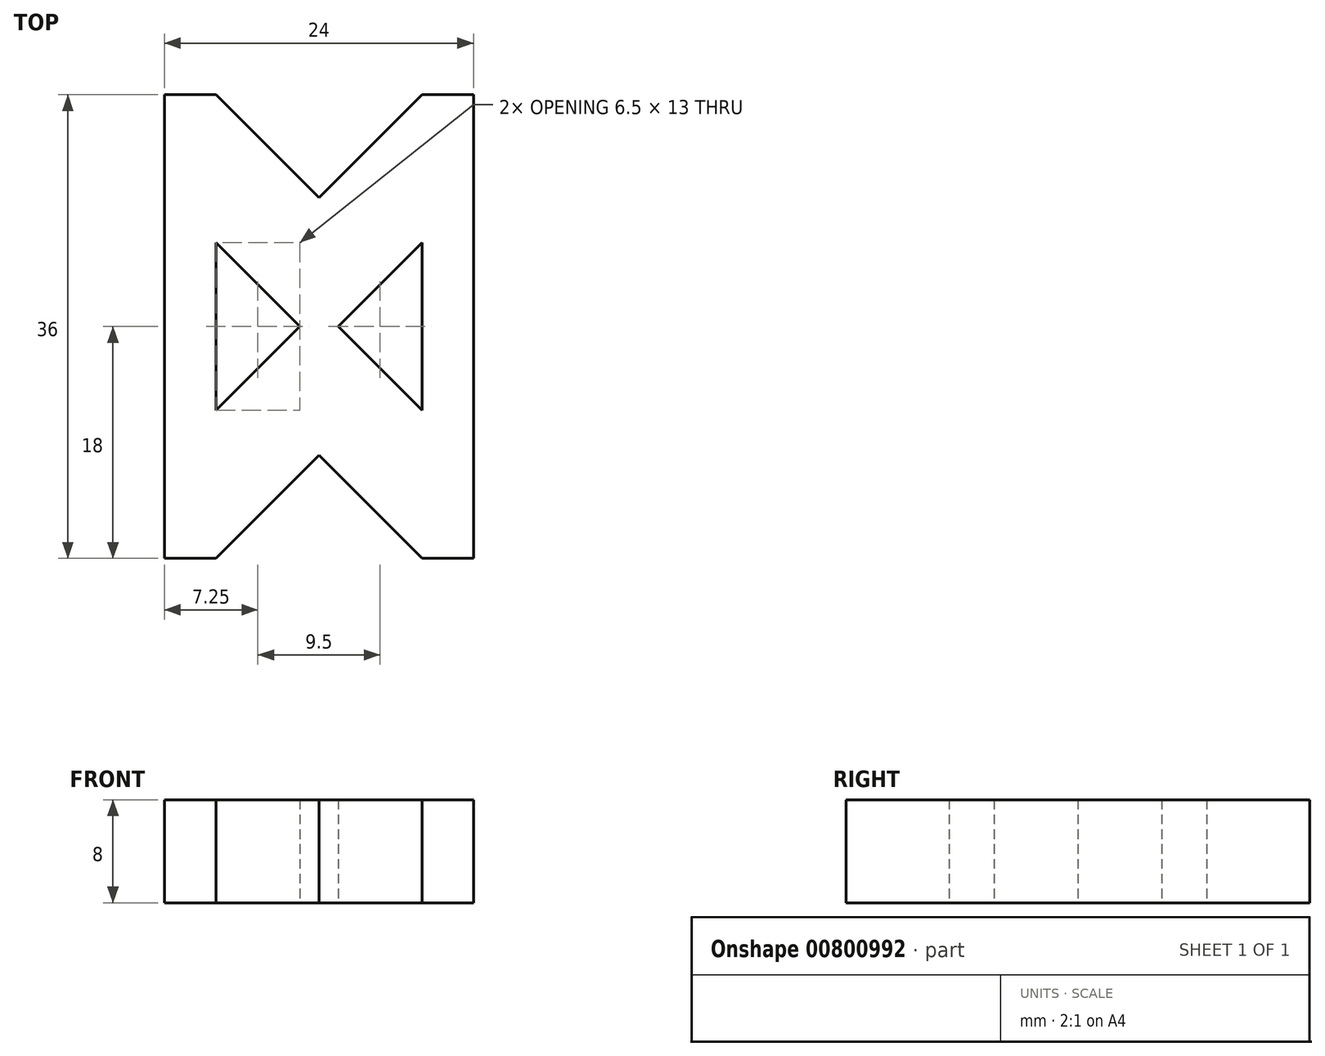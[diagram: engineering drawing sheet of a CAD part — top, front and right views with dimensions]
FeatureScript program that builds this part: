
annotation { "Feature Type Name" : "Feature", "Feature Type Description" : "" }
export const myFeature = defineFeature(function(context is Context, id is Id, definition is map)
    precondition{}
    {
        {
            var Q0;
            Q0=qCreatedBy(makeId("Top.planeOp"),FACE);
            var sketch = newSketch(context, id + "F0", { "sketchPlane" : qUnion([Q0])});
            skLineSegment(sketch, "E0", {"start": v(0, 0) * mm, "end": v(0, -36) * mm});
            skLineSegment(sketch, "E1", {"start": v(0, -36) * mm, "end": v(4, -36) * mm});
            skLineSegment(sketch, "E2", {"start": v(4, -36) * mm, "end": v(12, -28) * mm});
            skLineSegment(sketch, "E3", {"start": v(12, -28) * mm, "end": v(20, -36) * mm});
            skLineSegment(sketch, "E4", {"start": v(20, -36) * mm, "end": v(24, -36) * mm});
            skLineSegment(sketch, "E5", {"start": v(24, -36) * mm, "end": v(24, 0) * mm});
            skLineSegment(sketch, "E6", {"start": v(24, 0) * mm, "end": v(20, 0) * mm});
            skLineSegment(sketch, "E7", {"start": v(20, 0) * mm, "end": v(12, -8) * mm});
            skLineSegment(sketch, "E8", {"start": v(12, -8) * mm, "end": v(4, 0) * mm});
            skLineSegment(sketch, "E9", {"start": v(4, 0) * mm, "end": v(0, 0) * mm});
            skLineSegment(sketch, "E10", {"start": v(4, -11.5) * mm, "end": v(4, -24.5) * mm});
            skLineSegment(sketch, "E11", {"start": v(12, -8) * mm, "end": v(12, -28) * mm, "construction": true});
            skLineSegment(sketch, "E12.MirrorCS", {"start": v(13.5, -18) * mm, "end": v(20, -11.5) * mm});
            skLineSegment(sketch, "E13.MirrorCS", {"start": v(20, -11.5) * mm, "end": v(20, -24.5) * mm});
            skLineSegment(sketch, "E14", {"start": v(4, -11.5) * mm, "end": v(10.5, -18) * mm});
            skLineSegment(sketch, "E15", {"start": v(10.5, -18) * mm, "end": v(4, -24.5) * mm});
            skLineSegment(sketch, "E16", {"start": v(10.5, -18) * mm, "end": v(13.5, -18) * mm, "construction": true});
            skLineSegment(sketch, "E17", {"start": v(13.5, -18) * mm, "end": v(20, -24.5) * mm});
            skLineSegment(sketch, "E18", {"start": v(4, -11.5) * mm, "end": v(4, 0) * mm, "construction": true});
            skLineSegment(sketch, "E19", {"start": v(4, -24.5) * mm, "end": v(4, -36) * mm, "construction": true});
            skSolve(sketch);
        }
        {
            var Q0;
            Q0=makeQuery(id+"F0.imprint","IMPRINT",FACE,{"disambiguationData":[TD([[makeQuery(id+"F0.imprint","IMPRINT",EDGE,{"derivedFrom":sQuery(id+"F0.wireOp",EDGE,"E0")}),1.0]])]});
            extrude(context, id + "F1", {"entities" : qUnion([Q0]), "depth" : 8 * mm, "offsetDistance" : 25 * mm});
        }
    });
